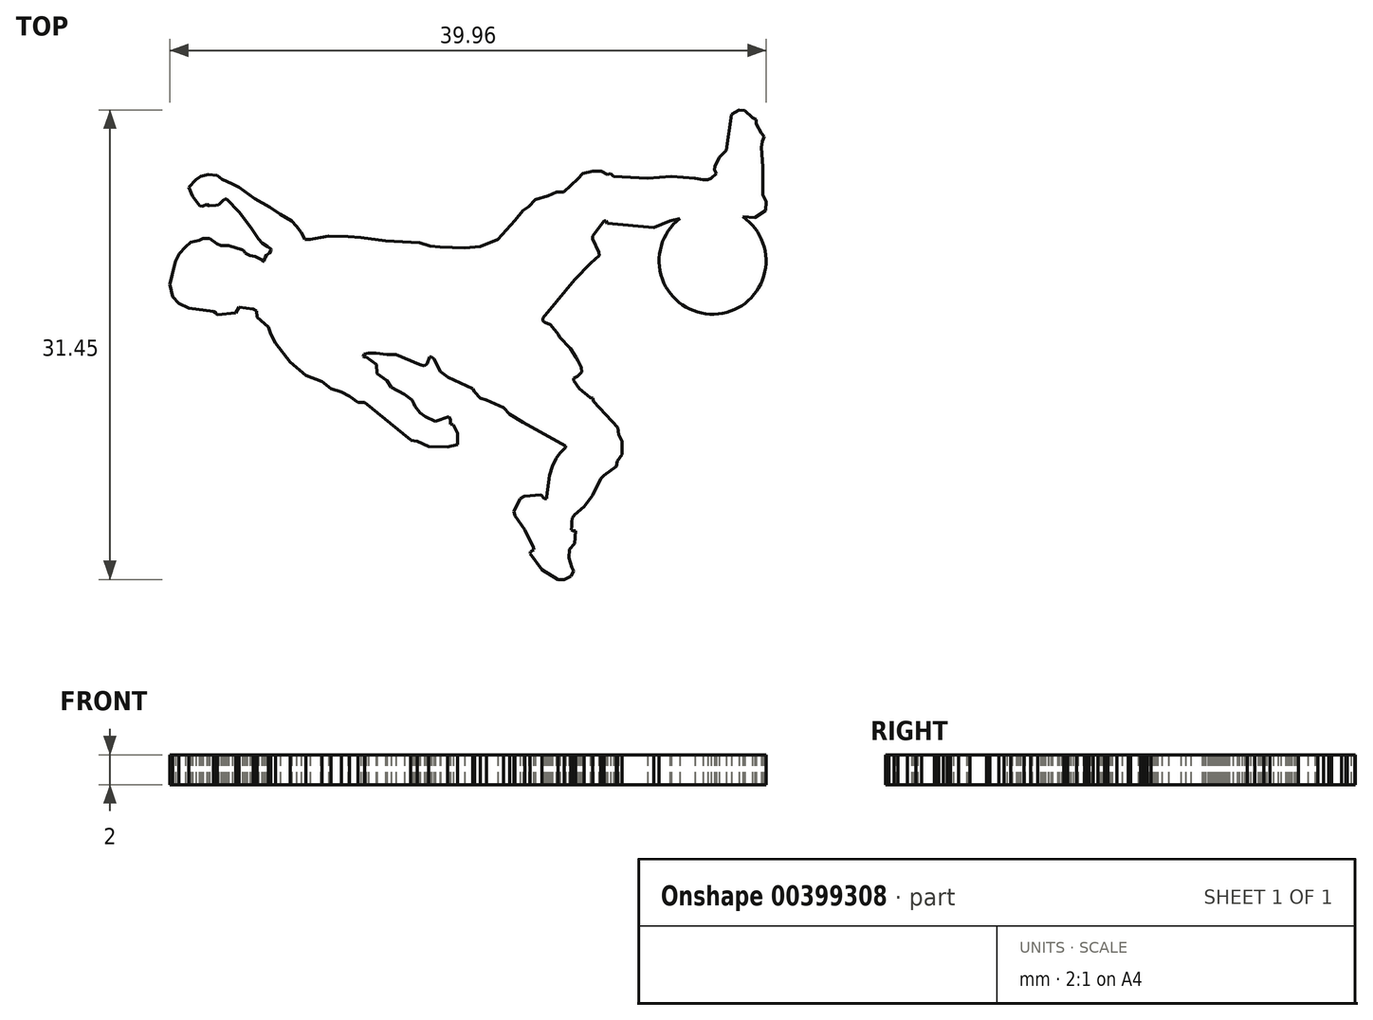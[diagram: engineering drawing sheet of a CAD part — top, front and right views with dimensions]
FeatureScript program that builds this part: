
annotation { "Feature Type Name" : "Feature", "Feature Type Description" : "" }
export const myFeature = defineFeature(function(context is Context, id is Id, definition is map)
    precondition{}
    {
        {
            var Q0;
            Q0=qCreatedBy(makeId("Top.planeOp"),FACE);
            var sketch = newSketch(context, id + "F0", { "sketchPlane" : qUnion([Q0])});
            skLineSegment(sketch, "E0", {"start": v(1.78, 4.9) * mm, "end": v(2.95, 5.39) * mm});
            skLineSegment(sketch, "E1", {"start": v(2.95, 5.39) * mm, "end": v(4.08, 6.66) * mm});
            skLineSegment(sketch, "E2", {"start": v(4.08, 6.66) * mm, "end": v(4.61, 7.32) * mm});
            skLineSegment(sketch, "E3", {"start": v(4.61, 7.32) * mm, "end": v(5.02, 7.6) * mm});
            skLineSegment(sketch, "E4", {"start": v(5.02, 7.6) * mm, "end": v(5.44, 8.06) * mm});
            skLineSegment(sketch, "E5", {"start": v(5.44, 8.06) * mm, "end": v(6.3, 8.31) * mm});
            skLineSegment(sketch, "E6", {"start": v(6.3, 8.31) * mm, "end": v(6.87, 8.58) * mm});
            skLineSegment(sketch, "E7", {"start": v(6.87, 8.58) * mm, "end": v(7.35, 8.58) * mm});
            skLineSegment(sketch, "E8", {"start": v(7.35, 8.58) * mm, "end": v(8.3, 9.47) * mm});
            skLineSegment(sketch, "E9", {"start": v(8.3, 9.47) * mm, "end": v(8.63, 9.82) * mm});
            skLineSegment(sketch, "E10", {"start": v(8.63, 9.82) * mm, "end": v(9.29, 9.97) * mm});
            skLineSegment(sketch, "E11", {"start": v(9.29, 9.97) * mm, "end": v(9.87, 9.97) * mm});
            skLineSegment(sketch, "E12", {"start": v(9.87, 9.97) * mm, "end": v(10.27, 9.75) * mm});
            skLineSegment(sketch, "E13", {"start": v(10.27, 9.75) * mm, "end": v(10.5, 9.82) * mm});
            skLineSegment(sketch, "E14", {"start": v(10.5, 9.82) * mm, "end": v(10.68, 9.63) * mm});
            skLineSegment(sketch, "E15", {"start": v(10.68, 9.63) * mm, "end": v(12.96, 9.5) * mm});
            skLineSegment(sketch, "E16", {"start": v(12.96, 9.5) * mm, "end": v(14.57, 9.63) * mm});
            skLineSegment(sketch, "E17", {"start": v(14.57, 9.63) * mm, "end": v(16.16, 9.5) * mm});
            skLineSegment(sketch, "E18", {"start": v(16.16, 9.5) * mm, "end": v(16.68, 9.41) * mm});
            skLineSegment(sketch, "E19", {"start": v(16.68, 9.41) * mm, "end": v(17, 9.4) * mm});
            skLineSegment(sketch, "E20", {"start": v(17, 9.4) * mm, "end": v(17.24, 9.5) * mm});
            skLineSegment(sketch, "E21", {"start": v(17.24, 9.5) * mm, "end": v(17.5, 9.75) * mm});
            skLineSegment(sketch, "E22", {"start": v(17.5, 9.75) * mm, "end": v(17.58, 9.82) * mm});
            skLineSegment(sketch, "E23", {"start": v(17.58, 9.82) * mm, "end": v(17.44, 10.05) * mm});
            skLineSegment(sketch, "E24", {"start": v(17.44, 10.05) * mm, "end": v(17.5, 10.28) * mm});
            skLineSegment(sketch, "E25", {"start": v(17.5, 10.28) * mm, "end": v(17.78, 10.88) * mm});
            skLineSegment(sketch, "E26", {"start": v(17.78, 10.88) * mm, "end": v(18.25, 11.37) * mm});
            skLineSegment(sketch, "E27", {"start": v(18.25, 11.37) * mm, "end": v(18.6, 13.79) * mm});
            skLineSegment(sketch, "E28", {"start": v(18.6, 13.79) * mm, "end": v(19.1, 14.06) * mm});
            skLineSegment(sketch, "E29", {"start": v(19.1, 14.06) * mm, "end": v(19.49, 14.04) * mm});
            skLineSegment(sketch, "E30", {"start": v(19.49, 14.04) * mm, "end": v(20, 13.54) * mm});
            skLineSegment(sketch, "E31", {"start": v(20, 13.54) * mm, "end": v(20.25, 13.42) * mm});
            skLineSegment(sketch, "E32", {"start": v(20.25, 13.42) * mm, "end": v(20.23, 13.15) * mm});
            skLineSegment(sketch, "E33", {"start": v(20.23, 13.15) * mm, "end": v(20.58, 12.5) * mm});
            skLineSegment(sketch, "E34", {"start": v(20.58, 12.5) * mm, "end": v(20.8, 12.29) * mm});
            skLineSegment(sketch, "E35", {"start": v(20.8, 12.29) * mm, "end": v(20.64, 11.96) * mm});
            skLineSegment(sketch, "E36", {"start": v(20.64, 11.96) * mm, "end": v(20.58, 11.56) * mm});
            skLineSegment(sketch, "E37", {"start": v(20.58, 11.56) * mm, "end": v(20.69, 10.25) * mm});
            skLineSegment(sketch, "E38", {"start": v(20.69, 10.25) * mm, "end": v(20.69, 8.37) * mm});
            skLineSegment(sketch, "E39", {"start": v(20.69, 8.37) * mm, "end": v(20.92, 7.92) * mm});
            skLineSegment(sketch, "E40", {"start": v(20.92, 7.92) * mm, "end": v(20.9, 7.32) * mm});
            skLineSegment(sketch, "E41", {"start": v(20.9, 7.32) * mm, "end": v(20.14, 6.84) * mm});
            skLineSegment(sketch, "E42", {"start": v(20.14, 6.84) * mm, "end": v(19.36, 6.9) * mm});
            skLineSegment(sketch, "E43", {"start": v(15.13, 6.79) * mm, "end": v(14.45, 6.63) * mm});
            skLineSegment(sketch, "E44", {"start": v(14.45, 6.63) * mm, "end": v(13.38, 6.18) * mm});
            skLineSegment(sketch, "E45", {"start": v(13.38, 6.18) * mm, "end": v(10.27, 6.48) * mm});
            skLineSegment(sketch, "E46", {"start": v(10.27, 6.48) * mm, "end": v(10.18, 6.65) * mm});
            skLineSegment(sketch, "E47", {"start": v(10.18, 6.65) * mm, "end": v(10.04, 6.65) * mm});
            skLineSegment(sketch, "E48", {"start": v(10.04, 6.65) * mm, "end": v(9.29, 5.62) * mm});
            skLineSegment(sketch, "E49", {"start": v(9.29, 5.62) * mm, "end": v(9.28, 5.44) * mm});
            skLineSegment(sketch, "E50", {"start": v(9.28, 5.44) * mm, "end": v(9.7, 4.55) * mm});
            skLineSegment(sketch, "E51", {"start": v(9.7, 4.55) * mm, "end": v(9.73, 4.33) * mm});
            skLineSegment(sketch, "E52", {"start": v(9.73, 4.33) * mm, "end": v(9.17, 3.8) * mm});
            skLineSegment(sketch, "E53", {"start": v(9.17, 3.8) * mm, "end": v(8.08, 2.69) * mm});
            skLineSegment(sketch, "E54", {"start": v(8.08, 2.69) * mm, "end": v(6.89, 1.24) * mm});
            skLineSegment(sketch, "E55", {"start": v(6.89, 1.24) * mm, "end": v(5.97, 0.12) * mm});
            skLineSegment(sketch, "E56", {"start": v(5.97, 0.12) * mm, "end": v(5.97, -0.06) * mm});
            skLineSegment(sketch, "E57", {"start": v(5.97, -0.06) * mm, "end": v(6.1, -0.16) * mm});
            skLineSegment(sketch, "E58", {"start": v(6.1, -0.16) * mm, "end": v(6.47, -0.33) * mm});
            skLineSegment(sketch, "E59", {"start": v(6.47, -0.33) * mm, "end": v(7, -1) * mm});
            skLineSegment(sketch, "E60", {"start": v(7, -1) * mm, "end": v(7.07, -1.15) * mm});
            skLineSegment(sketch, "E61", {"start": v(7.07, -1.15) * mm, "end": v(7.8, -1.92) * mm});
            skLineSegment(sketch, "E62", {"start": v(7.8, -1.92) * mm, "end": v(8.2, -2.5) * mm});
            skLineSegment(sketch, "E63", {"start": v(8.2, -2.5) * mm, "end": v(8.32, -2.74) * mm});
            skLineSegment(sketch, "E64", {"start": v(8.32, -2.74) * mm, "end": v(8.53, -3.18) * mm});
            skLineSegment(sketch, "E65", {"start": v(8.53, -3.18) * mm, "end": v(8.56, -3.48) * mm});
            skLineSegment(sketch, "E66", {"start": v(8.56, -3.48) * mm, "end": v(8.26, -3.78) * mm});
            skLineSegment(sketch, "E67", {"start": v(8.26, -3.78) * mm, "end": v(8.02, -3.91) * mm});
            skLineSegment(sketch, "E68", {"start": v(8.02, -3.91) * mm, "end": v(8.02, -4.05) * mm});
            skLineSegment(sketch, "E69", {"start": v(8.02, -4.05) * mm, "end": v(8.4, -4.61) * mm});
            skLineSegment(sketch, "E70", {"start": v(8.4, -4.61) * mm, "end": v(9.12, -5.21) * mm});
            skLineSegment(sketch, "E71", {"start": v(9.12, -5.21) * mm, "end": v(9.29, -5.23) * mm});
            skLineSegment(sketch, "E72", {"start": v(9.29, -5.23) * mm, "end": v(9.34, -5.47) * mm});
            skLineSegment(sketch, "E73", {"start": v(9.34, -5.47) * mm, "end": v(10.98, -7.22) * mm});
            skLineSegment(sketch, "E74", {"start": v(10.98, -7.22) * mm, "end": v(11.02, -7.7) * mm});
            skLineSegment(sketch, "E75", {"start": v(11.02, -7.7) * mm, "end": v(11.26, -8.14) * mm});
            skLineSegment(sketch, "E76", {"start": v(11.26, -8.14) * mm, "end": v(11.26, -9.02) * mm});
            skLineSegment(sketch, "E77", {"start": v(11.26, -9.02) * mm, "end": v(10.94, -9.46) * mm});
            skLineSegment(sketch, "E78", {"start": v(10.94, -9.46) * mm, "end": v(10.89, -9.82) * mm});
            skLineSegment(sketch, "E79", {"start": v(10.89, -9.82) * mm, "end": v(10.04, -10.42) * mm});
            skLineSegment(sketch, "E80", {"start": v(10.04, -10.42) * mm, "end": v(9.82, -10.63) * mm});
            skLineSegment(sketch, "E81", {"start": v(9.82, -10.63) * mm, "end": v(9.3, -11.74) * mm});
            skLineSegment(sketch, "E82", {"start": v(9.3, -11.74) * mm, "end": v(8.73, -12.51) * mm});
            skLineSegment(sketch, "E83", {"start": v(8.73, -12.51) * mm, "end": v(8.1, -13.04) * mm});
            skLineSegment(sketch, "E84", {"start": v(8.1, -13.04) * mm, "end": v(7.92, -13.28) * mm});
            skLineSegment(sketch, "E85", {"start": v(7.92, -13.28) * mm, "end": v(7.88, -13.54) * mm});
            skLineSegment(sketch, "E86", {"start": v(7.88, -13.54) * mm, "end": v(7.88, -13.83) * mm});
            skLineSegment(sketch, "E87", {"start": v(7.88, -13.83) * mm, "end": v(7.85, -14.06) * mm});
            skLineSegment(sketch, "E88", {"start": v(7.85, -14.06) * mm, "end": v(8, -14.13) * mm});
            skLineSegment(sketch, "E89", {"start": v(8, -14.13) * mm, "end": v(8.14, -14.13) * mm});
            skLineSegment(sketch, "E90", {"start": v(8.14, -14.13) * mm, "end": v(8.1, -15) * mm});
            skLineSegment(sketch, "E91", {"start": v(8.1, -15) * mm, "end": v(7.72, -15.38) * mm});
            skLineSegment(sketch, "E92", {"start": v(7.72, -15.38) * mm, "end": v(7.7, -15.93) * mm});
            skLineSegment(sketch, "E93", {"start": v(7.7, -15.93) * mm, "end": v(7.88, -16.57) * mm});
            skLineSegment(sketch, "E94", {"start": v(7.88, -16.57) * mm, "end": v(8.03, -16.83) * mm});
            skLineSegment(sketch, "E95", {"start": v(8.03, -16.83) * mm, "end": v(7.84, -17.17) * mm});
            skLineSegment(sketch, "E96", {"start": v(7.84, -17.17) * mm, "end": v(7.37, -17.4) * mm});
            skLineSegment(sketch, "E97", {"start": v(7.37, -17.4) * mm, "end": v(6.98, -17.4) * mm});
            skLineSegment(sketch, "E98", {"start": v(6.98, -17.4) * mm, "end": v(5.9, -16.72) * mm});
            skLineSegment(sketch, "E99", {"start": v(5.9, -16.72) * mm, "end": v(5.11, -15.65) * mm});
            skLineSegment(sketch, "E100", {"start": v(5.11, -15.65) * mm, "end": v(5.12, -15.54) * mm});
            skLineSegment(sketch, "E101", {"start": v(5.12, -15.54) * mm, "end": v(5.34, -15.42) * mm});
            skLineSegment(sketch, "E102", {"start": v(5.34, -15.42) * mm, "end": v(5.33, -15.24) * mm});
            skLineSegment(sketch, "E103", {"start": v(5.33, -15.24) * mm, "end": v(4.76, -14.06) * mm});
            skLineSegment(sketch, "E104", {"start": v(4.76, -14.06) * mm, "end": v(4.08, -13.11) * mm});
            skLineSegment(sketch, "E105", {"start": v(4.08, -13.11) * mm, "end": v(4.02, -12.84) * mm});
            skLineSegment(sketch, "E106", {"start": v(4.02, -12.84) * mm, "end": v(4.14, -12.6) * mm});
            skLineSegment(sketch, "E107", {"start": v(4.14, -12.6) * mm, "end": v(4.27, -12.3) * mm});
            skLineSegment(sketch, "E108", {"start": v(4.27, -12.3) * mm, "end": v(4.43, -11.97) * mm});
            skLineSegment(sketch, "E109", {"start": v(4.43, -11.97) * mm, "end": v(4.73, -11.81) * mm});
            skLineSegment(sketch, "E110", {"start": v(4.73, -11.81) * mm, "end": v(5.83, -11.73) * mm});
            skLineSegment(sketch, "E111", {"start": v(5.83, -11.73) * mm, "end": v(6.07, -11.96) * mm});
            skLineSegment(sketch, "E112", {"start": v(6.07, -11.96) * mm, "end": v(6.2, -11.96) * mm});
            skLineSegment(sketch, "E113", {"start": v(6.2, -11.96) * mm, "end": v(6.21, -11.83) * mm});
            skLineSegment(sketch, "E114", {"start": v(6.21, -11.83) * mm, "end": v(6.3, -11.18) * mm});
            skLineSegment(sketch, "E115", {"start": v(6.3, -11.18) * mm, "end": v(6.41, -10.42) * mm});
            skLineSegment(sketch, "E116", {"start": v(6.41, -10.42) * mm, "end": v(6.58, -9.82) * mm});
            skLineSegment(sketch, "E117", {"start": v(6.58, -9.82) * mm, "end": v(6.83, -9.28) * mm});
            skLineSegment(sketch, "E118", {"start": v(6.83, -9.28) * mm, "end": v(7.09, -8.94) * mm});
            skLineSegment(sketch, "E119", {"start": v(7.09, -8.94) * mm, "end": v(7.4, -8.65) * mm});
            skLineSegment(sketch, "E120", {"start": v(7.4, -8.65) * mm, "end": v(7.5, -8.55) * mm});
            skLineSegment(sketch, "E121", {"start": v(7.5, -8.55) * mm, "end": v(7.47, -8.44) * mm});
            skLineSegment(sketch, "E122", {"start": v(7.47, -8.44) * mm, "end": v(6.88, -8.12) * mm});
            skLineSegment(sketch, "E123", {"start": v(6.88, -8.12) * mm, "end": v(4.61, -6.86) * mm});
            skLineSegment(sketch, "E124", {"start": v(4.61, -6.86) * mm, "end": v(3.75, -6.3) * mm});
            skLineSegment(sketch, "E125", {"start": v(3.75, -6.3) * mm, "end": v(3.31, -5.89) * mm});
            skLineSegment(sketch, "E126", {"start": v(3.31, -5.89) * mm, "end": v(2.17, -5.35) * mm});
            skLineSegment(sketch, "E127", {"start": v(2.17, -5.35) * mm, "end": v(1.75, -5.23) * mm});
            skLineSegment(sketch, "E128", {"start": v(1.75, -5.23) * mm, "end": v(1.38, -4.84) * mm});
            skLineSegment(sketch, "E129", {"start": v(1.38, -4.84) * mm, "end": v(1.25, -4.6) * mm});
            skLineSegment(sketch, "E130", {"start": v(1.25, -4.6) * mm, "end": v(-0.38, -3.84) * mm});
            skLineSegment(sketch, "E131", {"start": v(-0.38, -3.84) * mm, "end": v(-0.9, -3.46) * mm});
            skLineSegment(sketch, "E132", {"start": v(-0.9, -3.46) * mm, "end": v(-1.35, -2.61) * mm});
            skLineSegment(sketch, "E133", {"start": v(-1.35, -2.61) * mm, "end": v(-1.51, -2.5) * mm});
            skLineSegment(sketch, "E134", {"start": v(-1.51, -2.5) * mm, "end": v(-1.65, -2.5) * mm});
            skLineSegment(sketch, "E135", {"start": v(-1.65, -2.5) * mm, "end": v(-1.8, -2.91) * mm});
            skLineSegment(sketch, "E136", {"start": v(-1.8, -2.91) * mm, "end": v(-1.97, -3.08) * mm});
            skLineSegment(sketch, "E137", {"start": v(-1.97, -3.08) * mm, "end": v(-2.3, -3) * mm});
            skLineSegment(sketch, "E138", {"start": v(-2.3, -3) * mm, "end": v(-3.9, -2.32) * mm});
            skLineSegment(sketch, "E139", {"start": v(-3.9, -2.32) * mm, "end": v(-4.48, -2.32) * mm});
            skLineSegment(sketch, "E140", {"start": v(-4.48, -2.32) * mm, "end": v(-5.2, -2.22) * mm});
            skLineSegment(sketch, "E141", {"start": v(-5.2, -2.22) * mm, "end": v(-5.74, -2.22) * mm});
            skLineSegment(sketch, "E142", {"start": v(-5.74, -2.22) * mm, "end": v(-6.01, -2.27) * mm});
            skLineSegment(sketch, "E143", {"start": v(-6.01, -2.27) * mm, "end": v(-6.1, -2.44) * mm});
            skLineSegment(sketch, "E144", {"start": v(-6.1, -2.44) * mm, "end": v(-6.06, -2.47) * mm});
            skLineSegment(sketch, "E145", {"start": v(-6.06, -2.47) * mm, "end": v(-5.89, -2.48) * mm});
            skLineSegment(sketch, "E146", {"start": v(-5.89, -2.48) * mm, "end": v(-5.19, -3) * mm});
            skLineSegment(sketch, "E147", {"start": v(-5.19, -3) * mm, "end": v(-5.14, -3.6) * mm});
            skLineSegment(sketch, "E148", {"start": v(-5.14, -3.6) * mm, "end": v(-4.48, -4.08) * mm});
            skLineSegment(sketch, "E149", {"start": v(-4.48, -4.08) * mm, "end": v(-4.19, -4.5) * mm});
            skLineSegment(sketch, "E150", {"start": v(-4.19, -4.5) * mm, "end": v(-3.32, -4.99) * mm});
            skLineSegment(sketch, "E151", {"start": v(-3.32, -4.99) * mm, "end": v(-2.81, -5.36) * mm});
            skLineSegment(sketch, "E152", {"start": v(-2.81, -5.36) * mm, "end": v(-2.66, -5.63) * mm});
            skLineSegment(sketch, "E153", {"start": v(-2.66, -5.63) * mm, "end": v(-2.6, -5.77) * mm});
            skLineSegment(sketch, "E154", {"start": v(-2.6, -5.77) * mm, "end": v(-2.25, -6.22) * mm});
            skLineSegment(sketch, "E155", {"start": v(-2.25, -6.22) * mm, "end": v(-1.9, -6.48) * mm});
            skLineSegment(sketch, "E156", {"start": v(-1.9, -6.48) * mm, "end": v(-1.25, -6.79) * mm});
            skLineSegment(sketch, "E157", {"start": v(-1.68, -8.5) * mm, "end": v(-2.46, -8.13) * mm});
            skLineSegment(sketch, "E158", {"start": v(-2.46, -8.13) * mm, "end": v(-2.92, -8.07) * mm});
            skLineSegment(sketch, "E159", {"start": v(-2.92, -8.07) * mm, "end": v(-2.92, -8.05) * mm});
            skLineSegment(sketch, "E160", {"start": v(-2.92, -8.05) * mm, "end": v(-6, -5.53) * mm});
            skLineSegment(sketch, "E161", {"start": v(-6, -5.53) * mm, "end": v(-6.43, -5.53) * mm});
            skLineSegment(sketch, "E162", {"start": v(-6.43, -5.53) * mm, "end": v(-7, -5.11) * mm});
            skLineSegment(sketch, "E163", {"start": v(-7, -5.11) * mm, "end": v(-7.53, -4.82) * mm});
            skLineSegment(sketch, "E164", {"start": v(-7.53, -4.82) * mm, "end": v(-8.22, -4.6) * mm});
            skLineSegment(sketch, "E165", {"start": v(-8.22, -4.6) * mm, "end": v(-8.84, -4.14) * mm});
            skLineSegment(sketch, "E166", {"start": v(-8.84, -4.14) * mm, "end": v(-9.9, -3.72) * mm});
            skLineSegment(sketch, "E167", {"start": v(-9.9, -3.72) * mm, "end": v(-10.98, -2.83) * mm});
            skLineSegment(sketch, "E168", {"start": v(-10.98, -2.83) * mm, "end": v(-11.95, -1.57) * mm});
            skLineSegment(sketch, "E169", {"start": v(-11.95, -1.57) * mm, "end": v(-12.27, -0.97) * mm});
            skLineSegment(sketch, "E170", {"start": v(-12.27, -0.97) * mm, "end": v(-12.42, -0.47) * mm});
            skLineSegment(sketch, "E171", {"start": v(-12.42, -0.47) * mm, "end": v(-13.2, 0.2) * mm});
            skLineSegment(sketch, "E172", {"start": v(-13.2, 0.2) * mm, "end": v(-13.23, 0.61) * mm});
            skLineSegment(sketch, "E173", {"start": v(-13.23, 0.61) * mm, "end": v(-13.45, 0.73) * mm});
            skLineSegment(sketch, "E174", {"start": v(-13.45, 0.73) * mm, "end": v(-14.4, 0.84) * mm});
            skLineSegment(sketch, "E175", {"start": v(-14.4, 0.84) * mm, "end": v(-14.6, 0.46) * mm});
            skLineSegment(sketch, "E176", {"start": v(-14.6, 0.46) * mm, "end": v(-15.07, 0.42) * mm});
            skLineSegment(sketch, "E177", {"start": v(-15.07, 0.42) * mm, "end": v(-15.86, 0.36) * mm});
            skLineSegment(sketch, "E178", {"start": v(-15.86, 0.36) * mm, "end": v(-15.94, 0.48) * mm});
            skLineSegment(sketch, "E179", {"start": v(-15.94, 0.48) * mm, "end": v(-16.1, 0.56) * mm});
            skLineSegment(sketch, "E180", {"start": v(-16.1, 0.56) * mm, "end": v(-16.5, 0.62) * mm});
            skLineSegment(sketch, "E181", {"start": v(-16.5, 0.62) * mm, "end": v(-17.76, 0.8) * mm});
            skLineSegment(sketch, "E182", {"start": v(-17.76, 0.8) * mm, "end": v(-18.42, 1.1) * mm});
            skLineSegment(sketch, "E183", {"start": v(-18.42, 1.1) * mm, "end": v(-18.85, 1.56) * mm});
            skLineSegment(sketch, "E184", {"start": v(-18.85, 1.56) * mm, "end": v(-19.04, 2.38) * mm});
            skLineSegment(sketch, "E185", {"start": v(-19.04, 2.38) * mm, "end": v(-18.88, 3.06) * mm});
            skLineSegment(sketch, "E186", {"start": v(-18.88, 3.06) * mm, "end": v(-18.64, 3.93) * mm});
            skLineSegment(sketch, "E187", {"start": v(-18.64, 3.93) * mm, "end": v(-18.4, 4.44) * mm});
            skLineSegment(sketch, "E188", {"start": v(-18.4, 4.44) * mm, "end": v(-17.98, 4.87) * mm});
            skLineSegment(sketch, "E189", {"start": v(-17.98, 4.87) * mm, "end": v(-17.63, 5.2) * mm});
            skLineSegment(sketch, "E190", {"start": v(-17.63, 5.2) * mm, "end": v(-17.08, 5.32) * mm});
            skLineSegment(sketch, "E191", {"start": v(-17.08, 5.32) * mm, "end": v(-16.8, 5.47) * mm});
            skLineSegment(sketch, "E192", {"start": v(-16.8, 5.47) * mm, "end": v(-16.38, 5.47) * mm});
            skLineSegment(sketch, "E193", {"start": v(-16.38, 5.47) * mm, "end": v(-15.9, 5.12) * mm});
            skLineSegment(sketch, "E194", {"start": v(-15.9, 5.12) * mm, "end": v(-15.61, 4.99) * mm});
            skLineSegment(sketch, "E195", {"start": v(-15.61, 4.99) * mm, "end": v(-15.1, 4.99) * mm});
            skLineSegment(sketch, "E196", {"start": v(-15.1, 4.99) * mm, "end": v(-14.17, 4.7) * mm});
            skLineSegment(sketch, "E197", {"start": v(-14.17, 4.7) * mm, "end": v(-14.04, 4.6) * mm});
            skLineSegment(sketch, "E198", {"start": v(-14.04, 4.6) * mm, "end": v(-13.99, 4.47) * mm});
            skLineSegment(sketch, "E199", {"start": v(-13.99, 4.47) * mm, "end": v(-13.86, 4.4) * mm});
            skLineSegment(sketch, "E200", {"start": v(-13.86, 4.4) * mm, "end": v(-13.65, 4.3) * mm});
            skLineSegment(sketch, "E201", {"start": v(-13.65, 4.3) * mm, "end": v(-13.3, 4.27) * mm});
            skLineSegment(sketch, "E202", {"start": v(-13.3, 4.27) * mm, "end": v(-12.87, 4.03) * mm});
            skLineSegment(sketch, "E203", {"start": v(-12.87, 4.03) * mm, "end": v(-12.8, 3.93) * mm});
            skLineSegment(sketch, "E204", {"start": v(-12.8, 3.93) * mm, "end": v(-12.7, 3.94) * mm});
            skLineSegment(sketch, "E205", {"start": v(-12.7, 3.94) * mm, "end": v(-12.7, 4) * mm});
            skLineSegment(sketch, "E206", {"start": v(-12.7, 4) * mm, "end": v(-12.64, 4.2) * mm});
            skLineSegment(sketch, "E207", {"start": v(-12.64, 4.2) * mm, "end": v(-12.56, 4.36) * mm});
            skLineSegment(sketch, "E208", {"start": v(-12.56, 4.36) * mm, "end": v(-12.38, 4.48) * mm});
            skLineSegment(sketch, "E209", {"start": v(-12.38, 4.48) * mm, "end": v(-12.27, 4.63) * mm});
            skLineSegment(sketch, "E210", {"start": v(-12.27, 4.63) * mm, "end": v(-12.24, 4.69) * mm});
            skLineSegment(sketch, "E211", {"start": v(-12.24, 4.69) * mm, "end": v(-12.25, 4.77) * mm});
            skLineSegment(sketch, "E212", {"start": v(-12.25, 4.77) * mm, "end": v(-12.48, 4.93) * mm});
            skLineSegment(sketch, "E213", {"start": v(-12.48, 4.93) * mm, "end": v(-12.84, 5.15) * mm});
            skLineSegment(sketch, "E214", {"start": v(-12.84, 5.15) * mm, "end": v(-13.1, 5.44) * mm});
            skLineSegment(sketch, "E215", {"start": v(-13.1, 5.44) * mm, "end": v(-13.61, 6.18) * mm});
            skLineSegment(sketch, "E216", {"start": v(-13.61, 6.18) * mm, "end": v(-14.4, 7.23) * mm});
            skLineSegment(sketch, "E217", {"start": v(-14.4, 7.23) * mm, "end": v(-15.21, 8.1) * mm});
            skLineSegment(sketch, "E218", {"start": v(-15.21, 8.1) * mm, "end": v(-15.33, 8.1) * mm});
            skLineSegment(sketch, "E219", {"start": v(-15.33, 8.1) * mm, "end": v(-15.45, 8.04) * mm});
            skLineSegment(sketch, "E220", {"start": v(-15.45, 8.04) * mm, "end": v(-15.77, 7.71) * mm});
            skLineSegment(sketch, "E221", {"start": v(-15.77, 7.71) * mm, "end": v(-15.94, 7.67) * mm});
            skLineSegment(sketch, "E222", {"start": v(-15.94, 7.67) * mm, "end": v(-16.41, 7.64) * mm});
            skLineSegment(sketch, "E223", {"start": v(-16.41, 7.64) * mm, "end": v(-16.55, 7.74) * mm});
            skLineSegment(sketch, "E224", {"start": v(-16.55, 7.74) * mm, "end": v(-16.84, 7.62) * mm});
            skLineSegment(sketch, "E225", {"start": v(-16.84, 7.62) * mm, "end": v(-17.04, 7.63) * mm});
            skLineSegment(sketch, "E226", {"start": v(-17.04, 7.63) * mm, "end": v(-17.5, 8.3) * mm});
            skLineSegment(sketch, "E227", {"start": v(-17.5, 8.3) * mm, "end": v(-17.76, 8.9) * mm});
            skLineSegment(sketch, "E228", {"start": v(-17.76, 8.9) * mm, "end": v(-17.28, 9.38) * mm});
            skLineSegment(sketch, "E229", {"start": v(-17.28, 9.38) * mm, "end": v(-16.97, 9.63) * mm});
            skLineSegment(sketch, "E230", {"start": v(-16.97, 9.63) * mm, "end": v(-16.45, 9.75) * mm});
            skLineSegment(sketch, "E231", {"start": v(-16.45, 9.75) * mm, "end": v(-15.87, 9.68) * mm});
            skLineSegment(sketch, "E232", {"start": v(-15.87, 9.68) * mm, "end": v(-15.53, 9.43) * mm});
            skLineSegment(sketch, "E233", {"start": v(-15.53, 9.43) * mm, "end": v(-14.83, 9.1) * mm});
            skLineSegment(sketch, "E234", {"start": v(-14.83, 9.1) * mm, "end": v(-14.4, 8.9) * mm});
            skLineSegment(sketch, "E235", {"start": v(-14.4, 8.9) * mm, "end": v(-13.35, 8.14) * mm});
            skLineSegment(sketch, "E236", {"start": v(-13.35, 8.14) * mm, "end": v(-12.32, 7.57) * mm});
            skLineSegment(sketch, "E237", {"start": v(-12.32, 7.57) * mm, "end": v(-11.64, 7.07) * mm});
            skLineSegment(sketch, "E238", {"start": v(-11.64, 7.07) * mm, "end": v(-10.88, 6.65) * mm});
            skLineSegment(sketch, "E239", {"start": v(-10.88, 6.65) * mm, "end": v(-10.55, 6.28) * mm});
            skLineSegment(sketch, "E240", {"start": v(-10.55, 6.28) * mm, "end": v(-10.24, 5.88) * mm});
            skLineSegment(sketch, "E241", {"start": v(-10.24, 5.88) * mm, "end": v(-9.98, 5.4) * mm});
            skLineSegment(sketch, "E242", {"start": v(-9.98, 5.4) * mm, "end": v(-9.65, 5.39) * mm});
            skLineSegment(sketch, "E243", {"start": v(-9.65, 5.39) * mm, "end": v(-8.94, 5.53) * mm});
            skLineSegment(sketch, "E244", {"start": v(-8.94, 5.53) * mm, "end": v(-8.38, 5.62) * mm});
            skLineSegment(sketch, "E245", {"start": v(-8.38, 5.62) * mm, "end": v(-7.1, 5.58) * mm});
            skLineSegment(sketch, "E246", {"start": v(-7.1, 5.58) * mm, "end": v(-6.25, 5.53) * mm});
            skLineSegment(sketch, "E247", {"start": v(-6.25, 5.53) * mm, "end": v(-4.6, 5.3) * mm});
            skLineSegment(sketch, "E248", {"start": v(-4.6, 5.3) * mm, "end": v(-2.29, 5.17) * mm});
            skLineSegment(sketch, "E249", {"start": v(-2.29, 5.17) * mm, "end": v(-1.6, 4.96) * mm});
            skLineSegment(sketch, "E250", {"start": v(-1.6, 4.96) * mm, "end": v(-0.94, 4.88) * mm});
            skLineSegment(sketch, "E251", {"start": v(-0.94, 4.88) * mm, "end": v(0.71, 4.83) * mm});
            skLineSegment(sketch, "E252", {"start": v(0.71, 4.83) * mm, "end": v(1.78, 4.9) * mm});
            skArc(sketch, "E253", {"start": v(15.13, 6.79) * mm, "mid": v(17.42, 0.38) * mm, "end": v(19.36, 6.9) * mm});
            skLineSegment(sketch, "E254", {"start": v(-1.68, -8.5) * mm, "end": v(-0.41, -8.5) * mm});
            skLineSegment(sketch, "E255", {"start": v(-0.41, -8.5) * mm, "end": v(0.24, -8.36) * mm});
            skLineSegment(sketch, "E256", {"start": v(0.24, -8.36) * mm, "end": v(0.24, -7.58) * mm});
            skLineSegment(sketch, "E257", {"start": v(-1.25, -6.79) * mm, "end": v(-0.33, -6.5) * mm});
            skLineSegment(sketch, "E258", {"start": v(0.24, -7.58) * mm, "end": v(-0.05, -7.03) * mm});
            skLineSegment(sketch, "E259", {"start": v(-0.05, -7.03) * mm, "end": v(-0.23, -6.98) * mm});
            skLineSegment(sketch, "E260", {"start": v(-0.23, -6.98) * mm, "end": v(-0.22, -6.7) * mm});
            skLineSegment(sketch, "E261.trimOffspring", {"start": v(-0.22, -6.7) * mm, "end": v(-0.33, -6.5) * mm});
            skSolve(sketch);
        }
        {
            var Q0;
            {var subQ0=sQuery(id+"F0.wireOp",EDGE,"E156");Q0=makeQuery(id+"F0.imprint","IMPRINT",FACE,{"disambiguationData":[TD([[makeQuery(id+"F0.imprint","IMPRINT",EDGE,{"derivedFrom":subQ0}),1.0]])]});}
            var Q1;
            Q1=makeQuery(id+"F0.imprint","IMPRINT",FACE,{"disambiguationData":[TD([[makeQuery(id+"F0.imprint","IMPRINT",EDGE,{"derivedFrom":sQuery(id+"F0.wireOp",EDGE,"E0")}),-1.0]])]});
            extrude(context, id + "F1", {"entities" : qUnion([Q0, Q1]), "depth" : 2 * mm, "offsetDistance" : 25 * mm});
        }
    });
